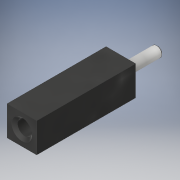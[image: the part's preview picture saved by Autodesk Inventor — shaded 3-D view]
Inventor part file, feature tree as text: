
AUTODESK INVENTOR PART (.ipt)
format: ipt  version: 2017 (Build 210142000, 142)  size: 122,368 bytes
history: native  units: in
note: dims shown in document units (in); Inventor stores cm internally (conversion verified against a paired STEP export)
features: extrude x3, sketch x3, chamfer x2
ambient origin geometry x8: Origin, YZ Plane, XZ Plane, XY Plane, X Axis, Y Axis, Z Axis, Center Point
bodies: Solid1 (feature_tree)
feature tree (8):
  extrude  "Extrusion1"  Depth=0.1in
  chamfer  "Chamfer1"  Distance=0.3346in
  extrude  "Extrusion2"  Depth=0.126in TaperAngle=0.0deg
  extrude  "Extrusion4"  Depth=0.126in TaperAngle=0.0deg
  chamfer  "Chamfer3"  Distance=0.005in Angle=45.0deg
  sketch  "Sketch1"  dims[d0=0.1in d1=0.1in d2=0.3346in d3=0.0in]
  sketch  "Sketch2"  dims[d4=0.01in d5=0.125in d6=45.0deg d7=0.126in d8=0.0in]
  sketch  "Sketch4"  dims[d15=0.035in d16=0.126in d17=0.0in d18=0.005in d19=0.125in d20=45.0deg]
